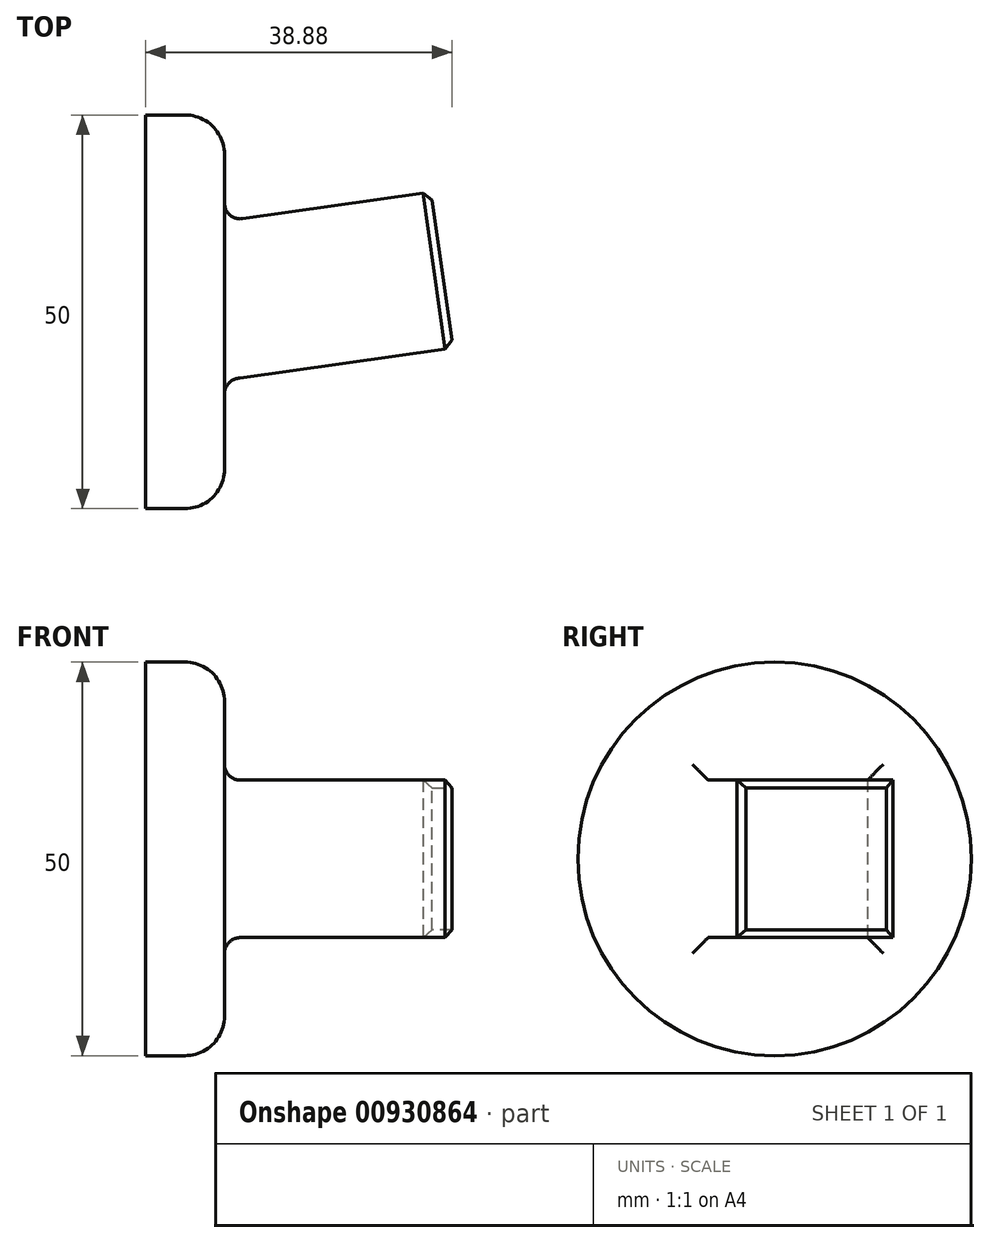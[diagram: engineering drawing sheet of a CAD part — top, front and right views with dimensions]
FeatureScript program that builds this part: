
annotation { "Feature Type Name" : "Feature", "Feature Type Description" : "" }
export const myFeature = defineFeature(function(context is Context, id is Id, definition is map)
    precondition{}
    {
        {
            var Q0;
            Q0=qCreatedBy(makeId("Right.planeOp"),FACE);
            var sketch = newSketch(context, id + "F0", { "sketchPlane" : qUnion([Q0])});
            skCircle(sketch, "E0", {"center": v(0, 0) * mm, "radius": 25 * mm});
            skSolve(sketch);
        }
        {
            var Q0;
            Q0=makeQuery(id+"F0.imprint","IMPRINT",FACE,{"disambiguationData":[TD([[makeQuery(id+"F0.imprint","IMPRINT",EDGE,{"derivedFrom":sQuery(id+"F0.wireOp",EDGE,"E0")}),1.0]])]});
            var Q1;
            Q1=makeQuery(id+"F0.imprint","IMPRINT",FACE,{"disambiguationData":[TD([[makeQuery(id+"F0.imprint","IMPRINT",EDGE,{"derivedFrom":sQuery(id+"F0.wireOp",EDGE,"UVVwoxmI-bTAD-5DPk-EYJF-5ij70QGy97Ro.bottom")}),-1.0]])]});
            extrude(context, id + "F1", {"entities" : qUnion([Q0, Q1]), "depth" : 10 * mm, "offsetDistance" : 25 * mm});
        }
        {
            var Q0;
            Q0=qCreatedBy(makeId("Front.planeOp"),FACE);
            var sketch = newSketch(context, id + "F2", { "sketchPlane" : qUnion([Q0])});
            skLineSegment(sketch, "E1", {"start": v(0, 75.07) * mm, "end": v(0, -76.39) * mm, "construction": true});
            skSolve(sketch);
        }
        {
            var Q0;
            Q0=sQuery(id+"F2.wireOp",EDGE,"E1");
            cPlane(context, id + "F3", {"entities" : qUnion([Q0]), "cplaneType" : CPlaneType.LINE_ANGLE, "offset" : 25 * mm, "angle" : 8 * degree, "oppositeDirection" : true, "width" : 150 * mm, "height" : 150 * mm});
        }
        {
            var Q0;
            Q0=qCreatedBy(id+"F3.planeOp",FACE);
            cPlane(context, id + "F4", {"entities" : qUnion([Q0]), "cplaneType" : CPlaneType.OFFSET, "offset" : 7 * mm, "oppositeDirection" : true, "width" : 150 * mm, "height" : 150 * mm});
        }
        {
            var Q0;
            Q0=qCreatedBy(id+"F4.planeOp",FACE);
            var sketch = newSketch(context, id + "F5", { "sketchPlane" : qUnion([Q0])});
            skLineSegment(sketch, "E2.bottom", {"start": v(10, -10) * mm, "end": v(-10, -10) * mm});
            skLineSegment(sketch, "E2.top", {"start": v(10, 10) * mm, "end": v(-10, 10) * mm});
            skLineSegment(sketch, "E2.left", {"start": v(10, -10) * mm, "end": v(10, 10) * mm});
            skLineSegment(sketch, "E2.right", {"start": v(-10, -10) * mm, "end": v(-10, 10) * mm});
            skPoint(sketch, "E2.middle", {"position": v(0, 0) * mm});
            skSolve(sketch);
        }
        {
            var Q0;
            Q0=makeQuery(id+"F5.imprint","IMPRINT",FACE,{"disambiguationData":[TD([[makeQuery(id+"F5.imprint","IMPRINT",EDGE,{"derivedFrom":sQuery(id+"F5.wireOp",EDGE,"E2.bottom")}),-1.0]])]});
            extrude(context, id + "F6", {"entities" : qUnion([Q0]), "operationType" : NewBodyOperationType.ADD, "oppositeDirection" : true, "depth" : 31 * mm, "offsetDistance" : 25 * mm});
        }
        {
            var Q0;
            Q0=makeQuery(id+"F6.opExtrude","CAP_EDGE",EDGE,{"disambiguationData":[OSD([sQuery(id+"F5.wireOp",EDGE,"E2.left")])],"isStart":false});
            var Q1;
            Q1=makeQuery(id+"F6.opExtrude","CAP_EDGE",EDGE,{"disambiguationData":[OSD([sQuery(id+"F5.wireOp",EDGE,"E2.top")])],"isStart":false});
            var Q2;
            Q2=makeQuery(id+"F6.opExtrude","CAP_EDGE",EDGE,{"disambiguationData":[OSD([sQuery(id+"F5.wireOp",EDGE,"E2.right")])],"isStart":false});
            var Q3;
            Q3=makeQuery(id+"F6.opExtrude","CAP_EDGE",EDGE,{"disambiguationData":[OSD([sQuery(id+"F5.wireOp",EDGE,"E2.bottom")])],"isStart":false});
            chamfer(context, id + "F7", {"entities" : qUnion([Q0, Q1, Q2, Q3]), "width" : 1 * mm, "tangentPropagation" : true});
        }
        {
            var Q0;
            Q0=makeQuery(id+"F1.opExtrude","CAP_EDGE",EDGE,{"disambiguationData":[OSD([sQuery(id+"F0.wireOp",EDGE,"E0")])],"isStart":false});
            fillet(context, id + "F8", {"entities" : qUnion([Q0]), "radius" : 5 * mm, "tangentPropagation" : true, "allowEdgeOverflow" : false});
        }
        {
            var Q0;
            Q0=makeQuery(id+"F6.boolean.opBoolean","INTERSECT",EDGE,{"derivedFrom":[makeQuery(id+"F1.opExtrude","CAP_FACE",FACE,{"disambiguationData":[OSD([sQuery(id+"F0.wireOp",EDGE,"E0")])],"isStart":false}),makeQuery(id+"F6.opExtrude","SWEPT_FACE",FACE,{"disambiguationData":[OSD([sQuery(id+"F5.wireOp",EDGE,"E2.bottom")])]})]});
            var Q1;
            Q1=makeQuery(id+"F6.boolean.opBoolean","INTERSECT",EDGE,{"derivedFrom":[makeQuery(id+"F1.opExtrude","CAP_FACE",FACE,{"disambiguationData":[OSD([sQuery(id+"F0.wireOp",EDGE,"E0")])],"isStart":false}),makeQuery(id+"F6.opExtrude","SWEPT_FACE",FACE,{"disambiguationData":[OSD([sQuery(id+"F5.wireOp",EDGE,"E2.left")])]})]});
            var Q2;
            Q2=makeQuery(id+"F6.boolean.opBoolean","INTERSECT",EDGE,{"derivedFrom":[makeQuery(id+"F1.opExtrude","CAP_FACE",FACE,{"disambiguationData":[OSD([sQuery(id+"F0.wireOp",EDGE,"E0")])],"isStart":false}),makeQuery(id+"F6.opExtrude","SWEPT_FACE",FACE,{"disambiguationData":[OSD([sQuery(id+"F5.wireOp",EDGE,"E2.top")])]})]});
            var Q3;
            Q3=makeQuery(id+"F6.boolean.opBoolean","INTERSECT",EDGE,{"derivedFrom":[makeQuery(id+"F1.opExtrude","CAP_FACE",FACE,{"disambiguationData":[OSD([sQuery(id+"F0.wireOp",EDGE,"E0")])],"isStart":false}),makeQuery(id+"F6.opExtrude","SWEPT_FACE",FACE,{"disambiguationData":[OSD([sQuery(id+"F5.wireOp",EDGE,"E2.right")])]})]});
            fillet(context, id + "F9", {"entities" : qUnion([Q0, Q1, Q2, Q3]), "radius" : 2 * mm, "tangentPropagation" : true, "allowEdgeOverflow" : false});
        }
    });
